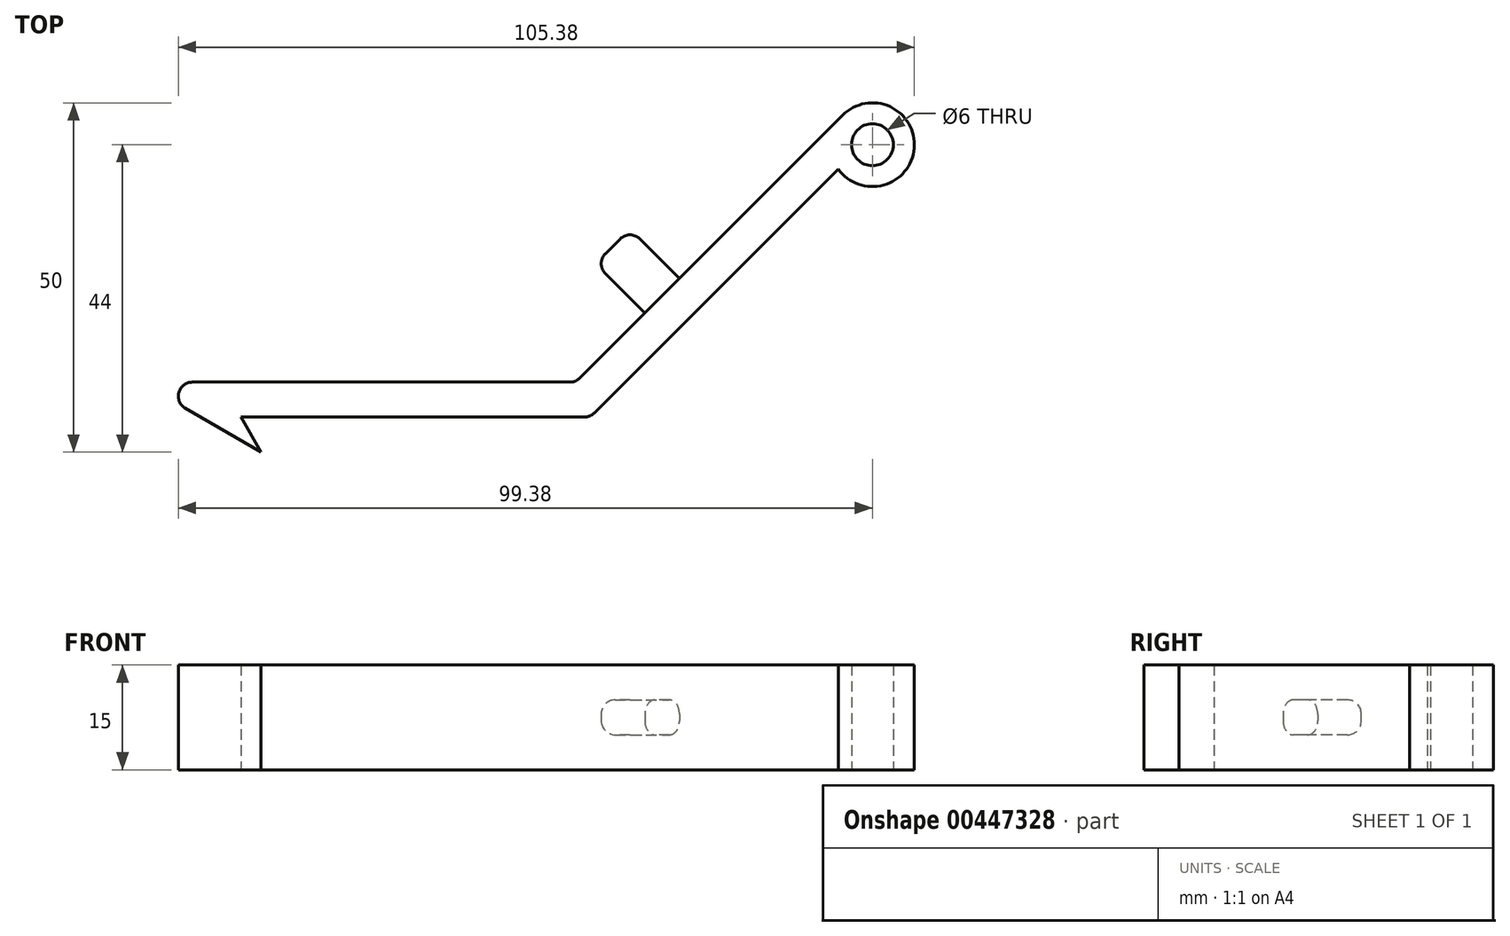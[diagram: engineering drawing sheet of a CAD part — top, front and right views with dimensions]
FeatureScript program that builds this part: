
annotation { "Feature Type Name" : "Feature", "Feature Type Description" : "" }
export const myFeature = defineFeature(function(context is Context, id is Id, definition is map)
    precondition{}
    {
        {
            var Q0;
            Q0=qCreatedBy(makeId("Top.planeOp"),FACE);
            var sketch = newSketch(context, id + "F0", { "sketchPlane" : qUnion([Q0])});
            skArc(sketch, "E0", {"start": v(-4.9, -3.48) * mm, "mid": v(5.98, -0.5) * mm, "end": v(-4.24, 4.24) * mm});
            skCircle(sketch, "E1", {"center": v(0, 0) * mm, "radius": 3 * mm});
            skLineSegment(sketch, "E2", {"start": v(-4.24, 4.24) * mm, "end": v(-42.49, -34) * mm});
            skLineSegment(sketch, "E3", {"start": v(-42.49, -34) * mm, "end": v(-104.85, -34) * mm});
            skLineSegment(sketch, "E4", {"start": v(-104.85, -34) * mm, "end": v(-87.53, -44) * mm});
            skLineSegment(sketch, "E5", {"start": v(-87.53, -44) * mm, "end": v(-90.41, -39) * mm});
            skLineSegment(sketch, "E6", {"start": v(-90.41, -39) * mm, "end": v(-40.41, -39) * mm});
            skLineSegment(sketch, "E7", {"start": v(-40.41, -39) * mm, "end": v(-4.9, -3.48) * mm});
            skLineSegment(sketch, "E8", {"start": v(0, 0) * mm, "end": v(0, -20.2) * mm, "construction": true});
            skLineSegment(sketch, "E9", {"start": v(-87.53, -44) * mm, "end": v(56.34, -44) * mm, "construction": true});
            skSolve(sketch);
        }
        {
            var Q0;
            Q0 = qSketchRegion(id + "F0", true);
            extrude(context, id + "F1", {"entities" : qUnion([Q0]), "depth" : 15 * mm});
        }
        {
            var Q0;
            Q0=makeQuery(id+"F1.opExtrude","SWEPT_FACE",FACE,{"disambiguationData":[OSD([sQuery(id+"F0.wireOp",EDGE,"E2")])]});
            var sketch = newSketch(context, id + "F2", { "sketchPlane" : qUnion([Q0])});
            skLineSegment(sketch, "E10.bottom", {"start": v(33.08, 10) * mm, "end": v(40.08, 10) * mm});
            skLineSegment(sketch, "E10.top", {"start": v(33.08, 5) * mm, "end": v(40.08, 5) * mm});
            skLineSegment(sketch, "E10.left", {"start": v(33.08, 10) * mm, "end": v(33.08, 5) * mm});
            skLineSegment(sketch, "E10.right", {"start": v(40.08, 10) * mm, "end": v(40.08, 5) * mm});
            skLineSegment(sketch, "E11", {"start": v(33.08, 7.5) * mm, "end": v(40.08, 7.5) * mm, "construction": true});
            skSolve(sketch);
        }
        {
            var Q0;
            Q0 = qSketchRegion(id + "F2", true);
            extrude(context, id + "F3", {"entities" : qUnion([Q0]), "operationType" : NewBodyOperationType.ADD, "depth" : 10 * mm});
        }
        {
            var Q0;
            Q0=makeQuery(id+"F3.opExtrude","CAP_EDGE",EDGE,{"disambiguationData":[OSD([sQuery(id+"F2.wireOp",EDGE,"E10.right")])],"isStart":true});
            var Q1;
            Q1=makeQuery(id+"F3.opExtrude","SWEPT_EDGE",EDGE,{"disambiguationData":[OSD([sQuery(id+"F2.wireOp",EDGE,"E10.bottom"),sQuery(id+"F2.wireOp",EDGE,"E10.right")])]});
            var Q2;
            Q2=makeQuery(id+"F3.opExtrude","SWEPT_EDGE",EDGE,{"disambiguationData":[OSD([sQuery(id+"F2.wireOp",EDGE,"E10.top"),sQuery(id+"F2.wireOp",EDGE,"E10.right")])]});
            var Q3;
            Q3=makeQuery(id+"F3.opExtrude","SWEPT_EDGE",EDGE,{"disambiguationData":[OSD([sQuery(id+"F2.wireOp",EDGE,"E10.top"),sQuery(id+"F2.wireOp",EDGE,"E10.left")])]});
            var Q4;
            Q4=makeQuery(id+"F3.opExtrude","SWEPT_EDGE",EDGE,{"disambiguationData":[OSD([sQuery(id+"F2.wireOp",EDGE,"E10.bottom"),sQuery(id+"F2.wireOp",EDGE,"E10.left")])]});
            var Q5;
            Q5=makeQuery(id+"F3.opExtrude","CAP_EDGE",EDGE,{"disambiguationData":[OSD([sQuery(id+"F2.wireOp",EDGE,"E10.bottom")])],"isStart":false});
            var Q6;
            Q6=makeQuery(id+"F3.opExtrude","CAP_EDGE",EDGE,{"disambiguationData":[OSD([sQuery(id+"F2.wireOp",EDGE,"E10.top")])],"isStart":false});
            var Q7;
            Q7=makeQuery(id+"F3.opExtrude","CAP_EDGE",EDGE,{"disambiguationData":[OSD([sQuery(id+"F2.wireOp",EDGE,"E10.left")])],"isStart":false});
            var Q8;
            Q8=makeQuery(id+"F3.opExtrude","CAP_EDGE",EDGE,{"disambiguationData":[OSD([sQuery(id+"F2.wireOp",EDGE,"E10.right")])],"isStart":false});
            fillet(context, id + "F4", {"entities" : qUnion([Q0, Q1, Q2, Q3, Q4, Q5, Q6, Q7, Q8]), "radius" : 2 * mm, "tangentPropagation" : true, "allowEdgeOverflow" : false});
        }
        {
            var Q0;
            Q0=makeQuery(id+"F1.opExtrude","SWEPT_EDGE",EDGE,{"disambiguationData":[OSD([sQuery(id+"F0.wireOp",EDGE,"E3"),sQuery(id+"F0.wireOp",EDGE,"E4")])]});
            var Q1;
            Q1=makeQuery(id+"F1.opExtrude","SWEPT_EDGE",EDGE,{"disambiguationData":[OSD([sQuery(id+"F0.wireOp",EDGE,"E6"),sQuery(id+"F0.wireOp",EDGE,"E7")])]});
            var Q2;
            Q2=makeQuery(id+"F1.opExtrude","SWEPT_EDGE",EDGE,{"disambiguationData":[OSD([sQuery(id+"F0.wireOp",EDGE,"E2"),sQuery(id+"F0.wireOp",EDGE,"E3")])]});
            fillet(context, id + "F5", {"entities" : qUnion([Q0, Q1, Q2]), "radius" : 2 * mm, "tangentPropagation" : true, "allowEdgeOverflow" : false});
        }
    });
